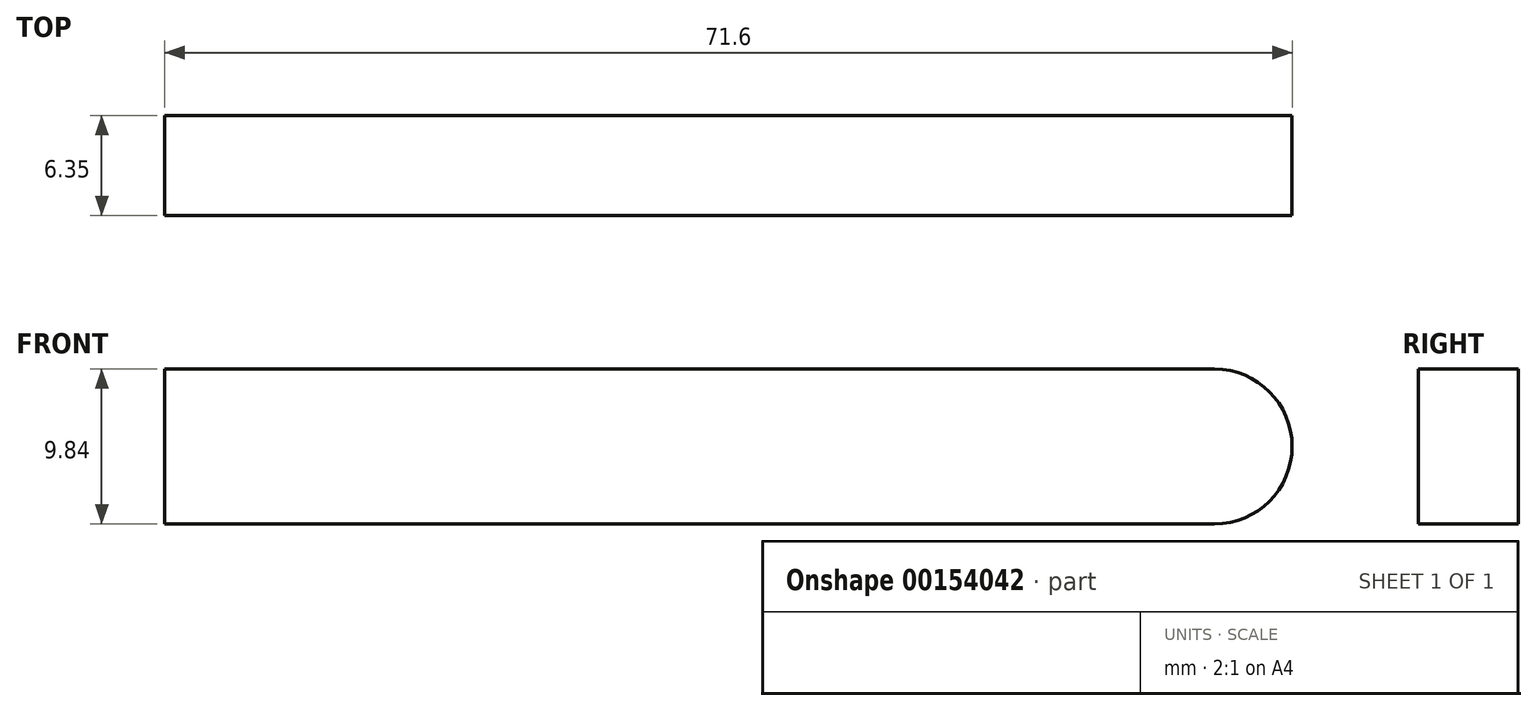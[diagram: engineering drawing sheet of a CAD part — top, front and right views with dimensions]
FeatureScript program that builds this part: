
annotation { "Feature Type Name" : "Feature", "Feature Type Description" : "" }
export const myFeature = defineFeature(function(context is Context, id is Id, definition is map)
    precondition{}
    {
        {
            var Q0;
            Q0=qCreatedBy(makeId("Front.planeOp"),FACE);
            var sketch = newSketch(context, id + "F0", { "sketchPlane" : qUnion([Q0])});
            skLineSegment(sketch, "E0.bottom", {"start": v(-35.56, 0) * mm, "end": v(31.12, 0) * mm});
            skLineSegment(sketch, "E0.top", {"start": v(-35.56, -9.84) * mm, "end": v(31.12, -9.84) * mm});
            skLineSegment(sketch, "E0.left", {"start": v(-35.56, 0) * mm, "end": v(-35.56, -9.84) * mm});
            skPoint(sketch, "E1.centerSnap0", {"position": v(31.12, -4.92) * mm});
            skArc(sketch, "E2", {"start": v(31.12, -9.84) * mm, "mid": v(36.04, -4.92) * mm, "end": v(31.12, 0) * mm});
            skSolve(sketch);
        }
        {
            var Q0;
            Q0=makeQuery(id+"F0.imprint","IMPRINT",FACE,{"disambiguationData":[TD([[makeQuery(id+"F0.imprint","IMPRINT",EDGE,{"derivedFrom":sQuery(id+"F0.wireOp",EDGE,"E0.bottom")}),-1.0]])]});
            extrude(context, id + "F1", {"entities" : qUnion([Q0]), "depth" : 6.35 * mm});
        }
    });
